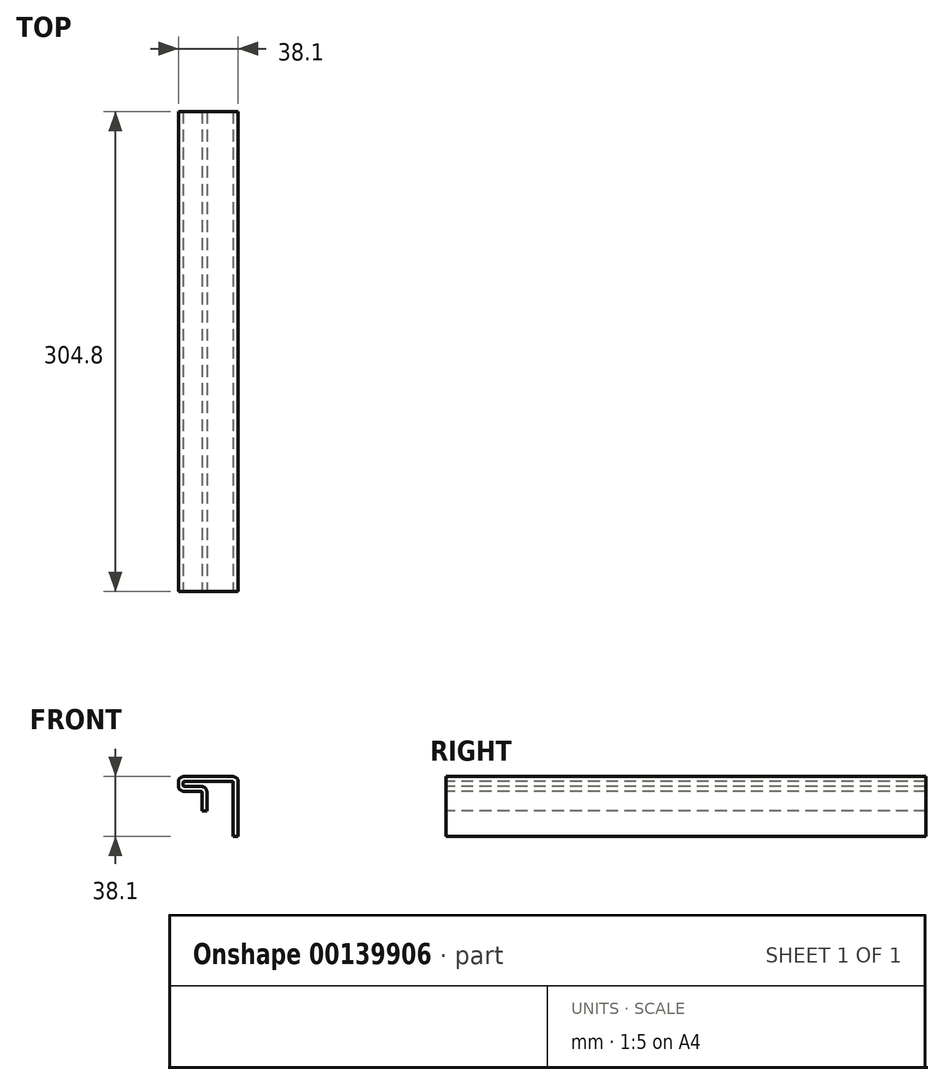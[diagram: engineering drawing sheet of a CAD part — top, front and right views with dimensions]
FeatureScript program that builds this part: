
annotation { "Feature Type Name" : "Feature", "Feature Type Description" : "" }
export const myFeature = defineFeature(function(context is Context, id is Id, definition is map)
    precondition{}
    {
        {
            var Q0;
            Q0=qCreatedBy(makeId("Front.planeOp"),FACE);
            var sketch = newSketch(context, id + "F0", { "sketchPlane" : qUnion([Q0])});
            skLineSegment(sketch, "E0", {"start": v(0, 0) * mm, "end": v(0, 38.1) * mm});
            skLineSegment(sketch, "E1", {"start": v(0, 38.1) * mm, "end": v(-38.1, 38.1) * mm});
            skLineSegment(sketch, "E2", {"start": v(-38.1, 38.1) * mm, "end": v(-38.1, 28.58) * mm});
            skLineSegment(sketch, "E3", {"start": v(-38.1, 28.58) * mm, "end": v(-23.12, 28.58) * mm});
            skLineSegment(sketch, "E4", {"start": v(-23.12, 28.58) * mm, "end": v(-23.12, 16.1) * mm});
            skLineSegment(sketch, "E5", {"start": v(-23.12, 16.1) * mm, "end": v(-19.94, 16.1) * mm});
            skLineSegment(sketch, "E6", {"start": v(-19.94, 16.1) * mm, "end": v(-19.94, 31.75) * mm});
            skLineSegment(sketch, "E7", {"start": v(-19.94, 31.75) * mm, "end": v(-34.93, 31.75) * mm});
            skLineSegment(sketch, "E8", {"start": v(-34.93, 31.75) * mm, "end": v(-34.93, 34.93) * mm});
            skLineSegment(sketch, "E9", {"start": v(-34.93, 34.93) * mm, "end": v(-3.18, 34.93) * mm});
            skLineSegment(sketch, "E10", {"start": v(-3.18, 34.93) * mm, "end": v(-3.17, 0) * mm});
            skLineSegment(sketch, "E11", {"start": v(-3.17, 0) * mm, "end": v(0, 0) * mm});
            skLineSegment(sketch, "E12", {"start": v(-34.93, 31.75) * mm, "end": v(-34.93, 28.58) * mm, "construction": true});
            skLineSegment(sketch, "E13", {"start": v(-34.93, 34.93) * mm, "end": v(-34.93, 38.1) * mm, "construction": true});
            skLineSegment(sketch, "E14", {"start": v(-34.93, 34.93) * mm, "end": v(-38.1, 34.93) * mm, "construction": true});
            skSolve(sketch);
        }
        {
            var Q0;
            Q0 = qSketchRegion(id + "F0", true);
            extrude(context, id + "F1", {"entities" : qUnion([Q0]), "oppositeDirection" : true, "depth" : 304.8 * mm});
        }
        {
            var Q0;
            Q0=makeQuery(id+"F1.opExtrude","SWEPT_EDGE",EDGE,{"disambiguationData":[OSD([sQuery(id+"F0.wireOp",EDGE,"E7"),sQuery(id+"F0.wireOp",EDGE,"E8")])]});
            var Q1;
            Q1=makeQuery(id+"F1.opExtrude","SWEPT_EDGE",EDGE,{"disambiguationData":[OSD([sQuery(id+"F0.wireOp",EDGE,"E8"),sQuery(id+"F0.wireOp",EDGE,"E9")])]});
            var Q2;
            Q2=makeQuery(id+"F1.opExtrude","SWEPT_EDGE",EDGE,{"disambiguationData":[OSD([sQuery(id+"F0.wireOp",EDGE,"E9"),sQuery(id+"F0.wireOp",EDGE,"E10")])]});
            var Q3;
            Q3=makeQuery(id+"F1.opExtrude","SWEPT_EDGE",EDGE,{"disambiguationData":[OSD([sQuery(id+"F0.wireOp",EDGE,"E3"),sQuery(id+"F0.wireOp",EDGE,"E4")])]});
            fillet(context, id + "F2", {"entities" : qUnion([Q0, Q1, Q2, Q3]), "radius" : 0.5 * mm, "tangentPropagation" : true, "allowEdgeOverflow" : false});
        }
        {
            var Q0;
            Q0=makeQuery(id+"F1.opExtrude","SWEPT_EDGE",EDGE,{"disambiguationData":[OSD([sQuery(id+"F0.wireOp",EDGE,"E1"),sQuery(id+"F0.wireOp",EDGE,"E2")])]});
            var Q1;
            Q1=makeQuery(id+"F1.opExtrude","SWEPT_EDGE",EDGE,{"disambiguationData":[OSD([sQuery(id+"F0.wireOp",EDGE,"E0"),sQuery(id+"F0.wireOp",EDGE,"E1")])]});
            var Q2;
            Q2=makeQuery(id+"F1.opExtrude","SWEPT_EDGE",EDGE,{"disambiguationData":[OSD([sQuery(id+"F0.wireOp",EDGE,"E6"),sQuery(id+"F0.wireOp",EDGE,"E7")])]});
            var Q3;
            Q3=makeQuery(id+"F1.opExtrude","SWEPT_EDGE",EDGE,{"disambiguationData":[OSD([sQuery(id+"F0.wireOp",EDGE,"E2"),sQuery(id+"F0.wireOp",EDGE,"E3")])]});
            fillet(context, id + "F3", {"entities" : qUnion([Q0, Q1, Q2, Q3]), "radius" : 3.68 * mm, "tangentPropagation" : true, "allowEdgeOverflow" : false});
        }
    });
